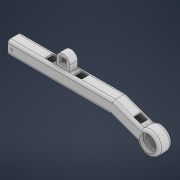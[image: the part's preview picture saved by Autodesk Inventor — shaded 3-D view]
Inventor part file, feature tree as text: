
AUTODESK INVENTOR PART (.ipt)
format: ipt  version: 2021 (Build 250183000, 183)  size: 535,552 bytes
history: native  units: mm
features: extrude x11, sketch x9, fillet x2, shell x1
ambient origin geometry x8: Origin, YZ Plane, XZ Plane, XY Plane, X Axis, Y Axis, Z Axis, Center Point
bodies: Volumenkörper1 (feature_tree)
feature tree (23):
  sketch  "Skizze1"  dims[d5=20.0mm d56=0.0mm]
  sketch  "Skizze4"  dims[d57=0.0mm d58=60.0mm]
  extrude  "Extrusion1"  TaperAngle=0.0deg  [1 undecoded]
  sketch  "Skizze13"  dims[d129=12.0mm d130=0.0mm d133=3.2mm]
  extrude  "Extrusion13"  Depth=60.0mm
  extrude  "Extrusion14"  Depth=20.0mm TaperAngle=0.0deg
  shell  "Wandung2"  Thickness=10.0mm
  extrude  "Extrusion11"  Depth=12.0mm
  extrude  "Extrusion12"  Depth=10.0mm TaperAngle=0.0deg
  extrude  "Extrusion15"  Depth=10.0mm
  fillet  "Rundung7"  Radius=10.0mm
  extrude  "Extrusion19"  Depth=50.0mm
  extrude  "Extrusion20"  Depth=10.0mm
  fillet  "Rundung8"  Radius=24.3mm
  extrude  "Extrusion21"  Depth=20.0mm TaperAngle=0.0deg
  extrude  "Extrusion22"  Depth=20.0mm TaperAngle=0.0deg
  extrude  "Extrusion23"  Depth=2.6mm
  sketch  "Skizze12"  dims[d74=20.0mm d75=20.0mm d78=10.0mm d79=20.0mm d80=0.0mm d116=10.0mm]
  sketch  "Skizze14"  dims[d135=6.0mm d136=10.0mm d137=0.0mm]
  sketch  "Skizze17"  dims[d138=160.0mm d140=3.490659mm d141=10.0mm]
  sketch  "Skizze18"  dims[d142=110.0mm d143=50.0mm]
  sketch  "Skizze19"  dims[d144=10.0mm d147=10.0mm d148=24.3mm]
  sketch  "Skizze20"  dims[d149=34.0mm d150=20.0mm d151=0.0mm d152=20.0mm d153=0.0mm d154=2.6mm d155=4.0mm d157=18.0mm d158=10.0mm d159=0.0mm d160=10.0mm d161=10.0mm d162=20.0mm d167=10.0mm d176=12.0mm d177=12.0mm d178=6.0mm d179=12.0mm d180=12.0mm d181=6.0mm d182=3.0mm d183=0.0mm d184=12.0mm d185=12.0mm d186=6.0mm d187=3.0mm d188=0.0mm d189=2.0mm d190=10.0mm d191=0.0mm d192=7.0mm d193=10.0mm d194=10.0mm d195=3.0mm d196=0.0mm d197=3.2mm d198=3.0mm d199=0.0mm d81=0.5mm d82=0.872665mm d83=0.5mm d84=0.872665mm]
note: 1 required parameter value undecoded (feature->parameter linkage not recoverable at this tier; creation-order binding heuristic only, values carry confidence <= 0.55)
